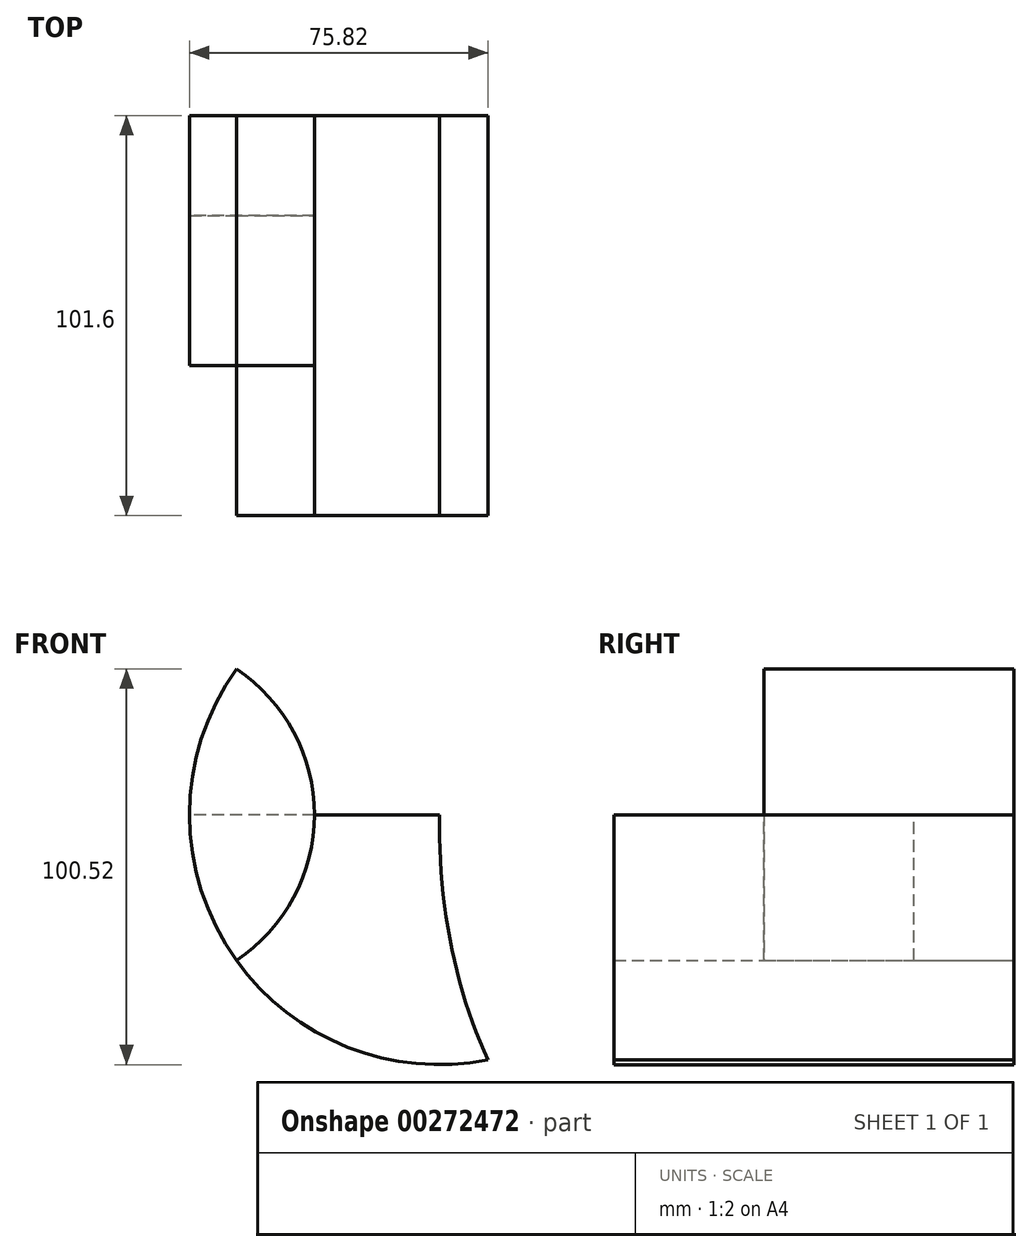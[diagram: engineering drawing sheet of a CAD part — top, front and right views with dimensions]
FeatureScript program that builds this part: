
annotation { "Feature Type Name" : "Feature", "Feature Type Description" : "" }
export const myFeature = defineFeature(function(context is Context, id is Id, definition is map)
    precondition{}
    {
        {
            var Q0;
            Q0=qCreatedBy(makeId("Front.planeOp"),FACE);
            var sketch = newSketch(context, id + "F0", { "sketchPlane" : qUnion([Q0])});
            skLineSegment(sketch, "E0", {"start": v(0, 0) * mm, "end": v(-76.2, 0) * mm});
            skCircle(sketch, "E1", {"center": v(-76.2, 0) * mm, "radius": 44.45 * mm});
            skLineSegment(sketch, "E2", {"start": v(-63.5, 0) * mm, "end": v(-31.75, 0) * mm});
            skCircle(sketch, "E3", {"center": v(0, 0) * mm, "radius": 63.5 * mm});
            skEllipse(sketch, "E4", {"center": v(63.5, 0) * mm, "majorRadius": 101.6 * mm, "minorRadius": 63.49 * mm, "majorAxis": v(0.03, 1)});
            skLineSegment(sketch, "E5", {"start": v(63.5, 0) * mm, "end": v(66.22, 101.56) * mm});
            skSolve(sketch);
        }
        {
            var Q0;
            {var subQ0=sQuery(id+"F0.wireOp",EDGE,"E3");var subQ1=sQuery(id+"F0.wireOp",EDGE,"E1");var subQ2=makeQuery(id+"F0.imprint","INTERSECT",VERTEX,{"disambiguationData":[OD(0.0)],"derivedFrom":[subQ1,subQ0]});Q0=makeQuery(id+"F0.imprint","IMPRINT",FACE,{"disambiguationData":[TD([[makeQuery(id+"F0.imprint","IMPRINT",EDGE,{"disambiguationData":[TD([[subQ2,-1.0]])],"derivedFrom":subQ1}),1.0]])]});}
            extrude(context, id + "F1", {"entities" : qUnion([Q0]), "depth" : 25.4 * mm});
        }
        {
            var Q0;
            {var subQ3=sQuery(id+"F0.wireOp",EDGE,"E1");var subQ5=sQuery(id+"F0.wireOp",EDGE,"E3");var subQ6=makeQuery(id+"F0.imprint","INTERSECT",VERTEX,{"disambiguationData":[OD(0.0)],"derivedFrom":[subQ3,subQ5]});Q0=makeQuery(id+"F0.imprint","IMPRINT",FACE,{"disambiguationData":[TD([[makeQuery(id+"F0.imprint","IMPRINT",EDGE,{"disambiguationData":[TD([[subQ6,1.0]])],"derivedFrom":subQ5}),1.0]])]});}
            var Q1;
            {var subQ3=sQuery(id+"F0.wireOp",EDGE,"E1");var subQ5=sQuery(id+"F0.wireOp",EDGE,"E3");var subQ6=makeQuery(id+"F0.imprint","INTERSECT",VERTEX,{"disambiguationData":[OD(1.0)],"derivedFrom":[subQ3,subQ5]});Q1=makeQuery(id+"F0.imprint","IMPRINT",FACE,{"disambiguationData":[TD([[makeQuery(id+"F0.imprint","IMPRINT",EDGE,{"disambiguationData":[TD([[subQ6,-1.0]])],"derivedFrom":subQ5}),1.0]])]});}
            var Q2;
            {var subQ0=sQuery(id+"F0.wireOp",EDGE,"E2");Q2=makeQuery(id+"F0.imprint","IMPRINT",FACE,{"disambiguationData":[TD([[makeQuery(id+"F0.imprint","IMPRINT",EDGE,{"derivedFrom":subQ0}),1.0]])]});}
            var Q3;
            {var subQ0=sQuery(id+"F0.wireOp",EDGE,"E2");Q3=makeQuery(id+"F0.imprint","IMPRINT",FACE,{"disambiguationData":[TD([[makeQuery(id+"F0.imprint","IMPRINT",EDGE,{"derivedFrom":subQ0}),-1.0]])]});}
            extrude(context, id + "F2", {"entities" : qUnion([Q0, Q1, Q2, Q3]), "depth" : 63.5 * mm});
        }
        {
            var Q0;
            {var subQ0=sQuery(id+"F0.wireOp",EDGE,"E4");var subQ1=sQuery(id+"F0.wireOp",EDGE,"E3");var subQ2=makeQuery(id+"F0.imprint","INTERSECT",VERTEX,{"disambiguationData":[OD(0.0)],"derivedFrom":[subQ1,subQ0]});Q0=makeQuery(id+"F0.imprint","IMPRINT",FACE,{"disambiguationData":[TD([[makeQuery(id+"F0.imprint","IMPRINT",EDGE,{"disambiguationData":[TD([[subQ2,1.0]])],"derivedFrom":subQ1}),-1.0]])]});}
            var Q1;
            {var subQ0=sQuery(id+"F0.wireOp",EDGE,"E4");var subQ1=sQuery(id+"F0.wireOp",EDGE,"E3");var subQ2=makeQuery(id+"F0.imprint","INTERSECT",VERTEX,{"disambiguationData":[OD(0.0)],"derivedFrom":[subQ1,subQ0]});Q1=makeQuery(id+"F0.imprint","IMPRINT",FACE,{"disambiguationData":[TD([[makeQuery(id+"F0.imprint","IMPRINT",EDGE,{"disambiguationData":[TD([[subQ2,1.0]])],"derivedFrom":subQ1}),1.0]])]});}
            extrude(context, id + "F3", {"entities" : qUnion([Q0, Q1]), "depth" : 101.6 * mm});
        }
    });
